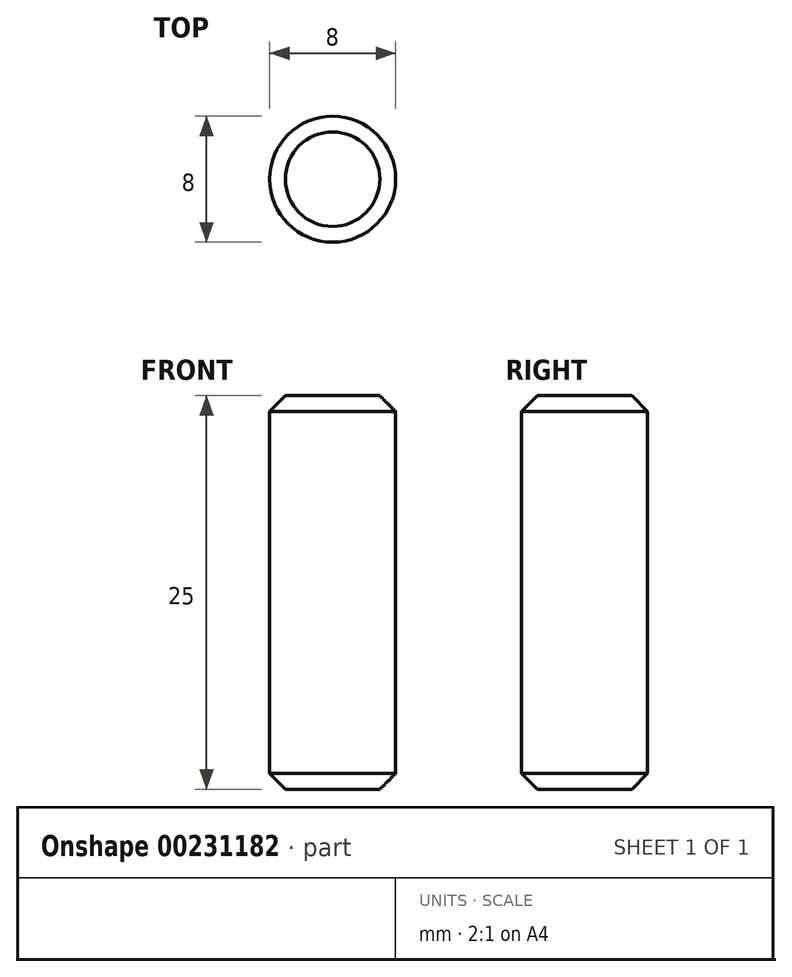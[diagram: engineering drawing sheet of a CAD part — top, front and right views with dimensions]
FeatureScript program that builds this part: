
annotation { "Feature Type Name" : "Feature", "Feature Type Description" : "" }
export const myFeature = defineFeature(function(context is Context, id is Id, definition is map)
    precondition{}
    {
        {
            var Q0;
            Q0=qCreatedBy(makeId("Top.planeOp"),FACE);
            var sketch = newSketch(context, id + "F0", { "sketchPlane" : qUnion([Q0])});
            skCircle(sketch, "E0", {"center": v(0, 0) * mm, "radius": 4 * mm});
            skSolve(sketch);
        }
        {
            var Q0;
            Q0 = qSketchRegion(id + "F0", true);
            extrude(context, id + "F1", {"entities" : qUnion([Q0]), "depth" : 25 * mm});
        }
        {
            var Q0;
            Q0=makeQuery(id+"F1.opExtrude","CAP_EDGE",EDGE,{"disambiguationData":[OSD([sQuery(id+"F0.wireOp",EDGE,"E0")])],"isStart":false});
            var Q1;
            Q1=makeQuery(id+"F1.opExtrude","CAP_EDGE",EDGE,{"disambiguationData":[OSD([sQuery(id+"F0.wireOp",EDGE,"E0")])],"isStart":true});
            chamfer(context, id + "F2", {"entities" : qUnion([Q0, Q1]), "chamferType" : ChamferType.OFFSET_ANGLE, "width" : 1 * mm, "oppositeDirection" : false, "angle" : 45 * degree, "tangentPropagation" : true});
        }
    });
